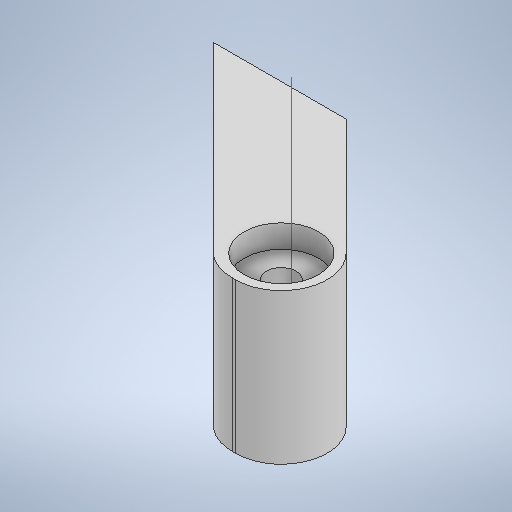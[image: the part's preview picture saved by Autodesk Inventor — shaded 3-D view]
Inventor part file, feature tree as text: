
AUTODESK INVENTOR PART (.ipt)
format: ipt  version: 2025 (Build 290162010, 162A)  size: 324,096 bytes
history: native  units: in
note: dims shown in document units (in); Inventor stores cm internally (conversion verified against a paired STEP export)
features: extrude x8, sketch x8, plane x1, fillet x1
ambient origin geometry x8: Origin, YZ Plane, XZ Plane, XY Plane, X Axis, Y Axis, Z Axis, Center Point
bodies: Volumenkörper1 (feature_tree)
feature tree (18):
  extrude  "Extrusion1"  TaperAngle=45.0deg  [1 undecoded]
  plane  "Arbeitsebene1"
  extrude  "Extrusion2"  Depth=1.2913in
  extrude  "Extrusion7"  Depth=1.2913in
  extrude  "Extrusion8"  Depth=1.9685in TaperAngle=0.0deg
  fillet  "Rundung2"  [1 undecoded]
  extrude  "Extrusion17"  Depth=0.0197in TaperAngle=0.0deg
  extrude  "Extrusion18"  Depth=0.3937in
  extrude  "Extrusion19"  Depth=0.3937in
  extrude  "Extrusion20"  Depth=0.0197in
  sketch  "Skizze1"  dims[d0=2.3622in d1=45.0deg]
  sketch  "Skizze2"  dims[d2=1.2913in d3=0.0in d5=0.1673in]
  sketch  "Skizze7"  dims[d7=1.2913in d8=0.5709in]
  sketch  "Skizze8"  dims[d10=0.7087in d11=1.9685in d12=0.0in d19=-0.4724in]
  sketch  "Skizze17"  dims[d39=0.3445in d40=0.0197in d41=0.7874in d42=0.0in d43=0.0in]
  sketch  "Skizze18"  dims[d44=0.3543in d45=0.0394in d46=0.0in d47=0.0in d82=0.3937in]
  sketch  "Skizze19"  dims[d85=0.6398in d86=0.3937in]
  sketch  "Skizze20"  dims[d87=0.3937in d89=0.4331in d90=0.3937in d91=0.0in d92=0.1969in d93=0.0in d94=0.1969in d95=0.0in d96=0.2559in d97=0.0in d98=0.0in d99=1.1417in d37=0.0197in d38=0.0344in]
note: 2 required parameter values undecoded (feature->parameter linkage not recoverable at this tier; creation-order binding heuristic only, values carry confidence <= 0.55)
